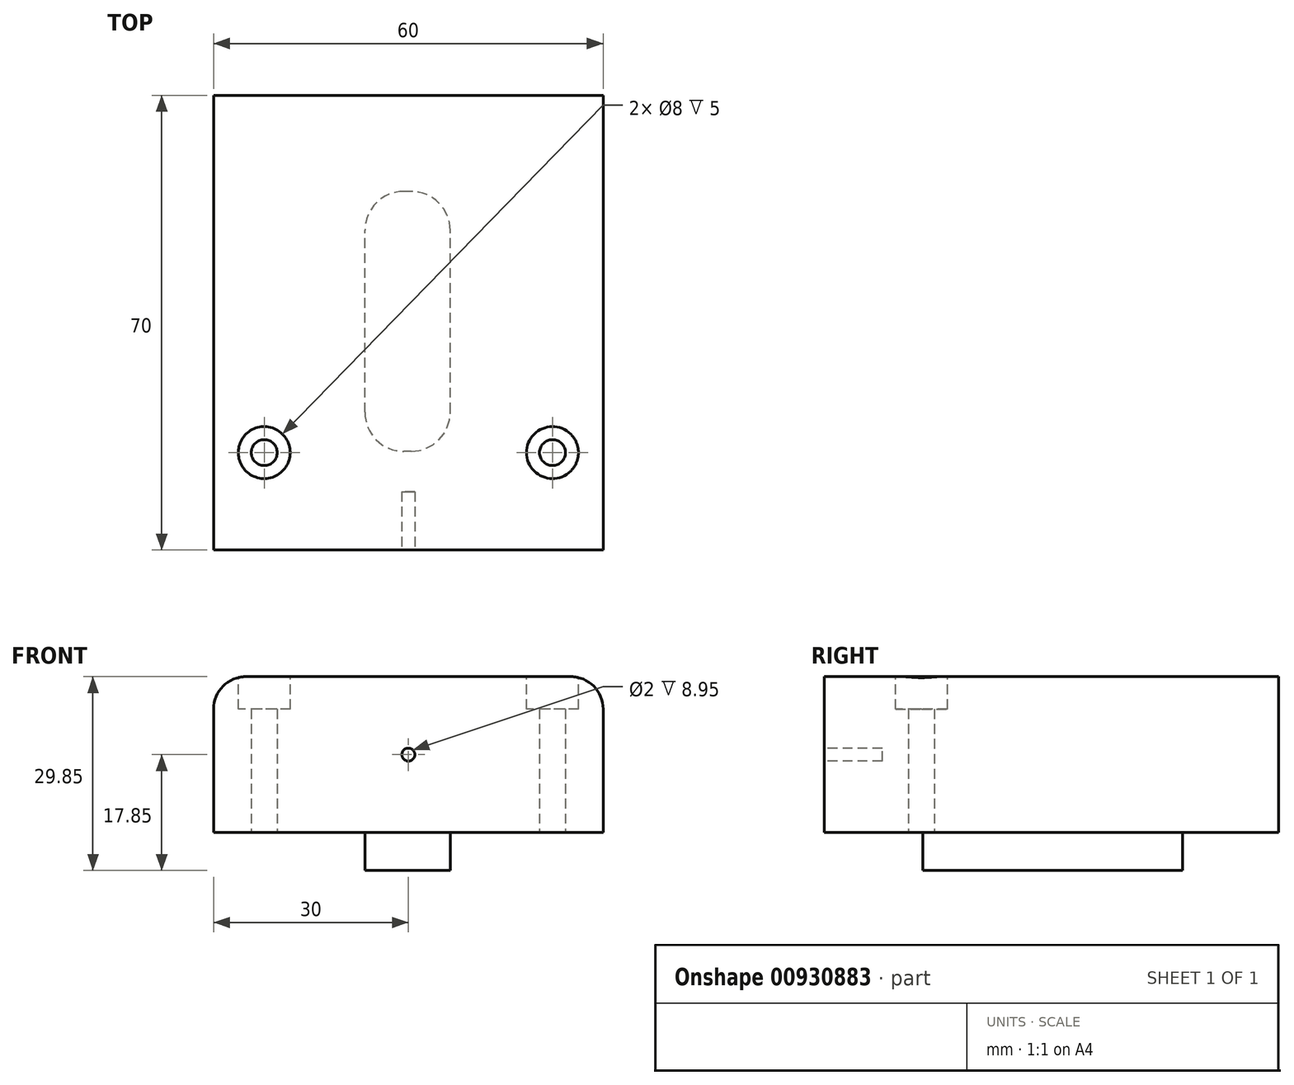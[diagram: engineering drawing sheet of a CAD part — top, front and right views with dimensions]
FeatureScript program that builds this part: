
annotation { "Feature Type Name" : "Feature", "Feature Type Description" : "" }
export const myFeature = defineFeature(function(context is Context, id is Id, definition is map)
    precondition{}
    {
        {
            var Q0;
            Q0=qCreatedBy(makeId("Top.planeOp"),FACE);
            var sketch = newSketch(context, id + "F0", { "sketchPlane" : qUnion([Q0])});
            skLineSegment(sketch, "E0.bottom", {"start": v(0, 0) * mm, "end": v(60, 0) * mm});
            skLineSegment(sketch, "E0.top", {"start": v(0, 70) * mm, "end": v(60, 70) * mm});
            skLineSegment(sketch, "E0.left", {"start": v(0, 0) * mm, "end": v(0, 70) * mm});
            skLineSegment(sketch, "E0.right", {"start": v(60, 0) * mm, "end": v(60, 70) * mm});
            skSolve(sketch);
        }
        {
            var Q0;
            Q0 = qSketchRegion(id + "F0", true);
            extrude(context, id + "F1", {"entities" : qUnion([Q0]), "depth" : 24 * mm, "offsetDistance" : 25 * mm});
        }
        {
            var Q0;
            Q0=makeQuery(id+"F1.opExtrude","CAP_EDGE",EDGE,{"disambiguationData":[OSD([sQuery(id+"F0.wireOp",EDGE,"E0.right")])],"isStart":false});
            var Q1;
            Q1=makeQuery(id+"F1.opExtrude","CAP_EDGE",EDGE,{"disambiguationData":[OSD([sQuery(id+"F0.wireOp",EDGE,"E0.left")])],"isStart":false});
            fillet(context, id + "F2", {"entities" : qUnion([Q0, Q1]), "radius" : 5 * mm, "tangentPropagation" : true, "allowEdgeOverflow" : false});
        }
        {
            var Q0;
            Q0=makeQuery(id+"F1.opExtrude","CAP_FACE",FACE,{"disambiguationData":[OSD([sQuery(id+"F0.wireOp",EDGE,"E0.bottom"),sQuery(id+"F0.wireOp",EDGE,"E0.top"),sQuery(id+"F0.wireOp",EDGE,"E0.left"),sQuery(id+"F0.wireOp",EDGE,"E0.right")])],"isStart":true});
            var sketch = newSketch(context, id + "F3", { "sketchPlane" : qUnion([Q0])});
            skCircle(sketch, "E1", {"center": v(7.8, -15) * mm, "radius": 2 * mm});
            skLineSegment(sketch, "E2", {"start": v(30, 0) * mm, "end": v(30, -70) * mm, "construction": true});
            skCircle(sketch, "E3.MirrorC", {"center": v(52.2, -15) * mm, "radius": 2 * mm});
            skSolve(sketch);
        }
        {
            var Q0;
            Q0 = qSketchRegion(id + "F3", true);
            extrude(context, id + "F4", {"entities" : qUnion([Q0]), "operationType" : NewBodyOperationType.REMOVE, "endBound" : BoundingType.THROUGH_ALL, "oppositeDirection" : true, "depth" : 25 * mm, "offsetDistance" : 25 * mm});
        }
        {
            var Q0;
            Q0=makeQuery(id+"F1.opExtrude","CAP_FACE",FACE,{"disambiguationData":[OSD([sQuery(id+"F0.wireOp",EDGE,"E0.bottom"),sQuery(id+"F0.wireOp",EDGE,"E0.top"),sQuery(id+"F0.wireOp",EDGE,"E0.left"),sQuery(id+"F0.wireOp",EDGE,"E0.right")])],"isStart":false});
            var sketch = newSketch(context, id + "F5", { "sketchPlane" : qUnion([Q0])});
            skCircle(sketch, "E4", {"center": v(52.2, 15) * mm, "radius": 4 * mm});
            skCircle(sketch, "E5", {"center": v(7.8, 15) * mm, "radius": 4 * mm});
            skSolve(sketch);
        }
        {
            var Q0;
            Q0 = qSketchRegion(id + "F5", true);
            extrude(context, id + "F6", {"entities" : qUnion([Q0]), "operationType" : NewBodyOperationType.REMOVE, "oppositeDirection" : true, "depth" : 5 * mm, "offsetDistance" : 25 * mm});
        }
        {
            var Q0;
            Q0=makeQuery(id+"F1.opExtrude","CAP_FACE",FACE,{"disambiguationData":[OSD([sQuery(id+"F0.wireOp",EDGE,"E0.bottom"),sQuery(id+"F0.wireOp",EDGE,"E0.top"),sQuery(id+"F0.wireOp",EDGE,"E0.left"),sQuery(id+"F0.wireOp",EDGE,"E0.right")])],"isStart":true});
            var sketch = newSketch(context, id + "F7", { "sketchPlane" : qUnion([Q0])});
            skLineSegment(sketch, "E6.bottom", {"start": v(36.45, -15.2) * mm, "end": v(23.3, -15.2) * mm});
            skLineSegment(sketch, "E6.top", {"start": v(36.45, -55.2) * mm, "end": v(23.3, -55.2) * mm});
            skLineSegment(sketch, "E6.left", {"start": v(36.45, -15.2) * mm, "end": v(36.45, -55.2) * mm});
            skLineSegment(sketch, "E6.right", {"start": v(23.3, -15.2) * mm, "end": v(23.3, -55.2) * mm});
            skSolve(sketch);
        }
        {
            var Q0;
            Q0 = qSketchRegion(id + "F7", true);
            extrude(context, id + "F8", {"entities" : qUnion([Q0]), "operationType" : NewBodyOperationType.ADD, "depth" : 5.85 * mm, "offsetDistance" : 25 * mm});
        }
        {
            var Q0;
            Q0=makeQuery(id+"F8.opExtrude","SWEPT_EDGE",EDGE,{"disambiguationData":[OSD([sQuery(id+"F7.wireOp",EDGE,"E6.top"),sQuery(id+"F7.wireOp",EDGE,"E6.right")])]});
            var Q1;
            Q1=makeQuery(id+"F8.opExtrude","SWEPT_EDGE",EDGE,{"disambiguationData":[OSD([sQuery(id+"F7.wireOp",EDGE,"E6.top"),sQuery(id+"F7.wireOp",EDGE,"E6.left")])]});
            var Q2;
            Q2=makeQuery(id+"F8.opExtrude","SWEPT_EDGE",EDGE,{"disambiguationData":[OSD([sQuery(id+"F7.wireOp",EDGE,"E6.bottom"),sQuery(id+"F7.wireOp",EDGE,"E6.left")])]});
            var Q3;
            Q3=makeQuery(id+"F8.opExtrude","SWEPT_EDGE",EDGE,{"disambiguationData":[OSD([sQuery(id+"F7.wireOp",EDGE,"E6.bottom"),sQuery(id+"F7.wireOp",EDGE,"E6.right")])]});
            fillet(context, id + "F9", {"entities" : qUnion([Q0, Q1, Q2, Q3]), "radius" : 6 * mm, "tangentPropagation" : true, "allowEdgeOverflow" : false});
        }
        {
            var Q0;
            Q0=makeQuery(id+"F1.opExtrude","SWEPT_FACE",FACE,{"disambiguationData":[OSD([sQuery(id+"F0.wireOp",EDGE,"E0.bottom")])]});
            var sketch = newSketch(context, id + "F10", { "sketchPlane" : qUnion([Q0])});
            skLineSegment(sketch, "E7", {"start": v(30, 0) * mm, "end": v(30, 24) * mm, "construction": true});
            skLineSegment(sketch, "E8", {"start": v(30, 0) * mm, "end": v(30, 12) * mm});
            skCircle(sketch, "E9", {"center": v(30, 12) * mm, "radius": 1 * mm});
            skSolve(sketch);
        }
        {
            var Q0;
            Q0 = qSketchRegion(id + "F10", true);
            extrude(context, id + "F11", {"entities" : qUnion([Q0]), "operationType" : NewBodyOperationType.REMOVE, "oppositeDirection" : true, "depth" : 8.95 * mm, "offsetDistance" : 25 * mm});
        }
    });
